# Revit family: Indoor_Pendant Lamp_Santa&Cole_M64
name_source: partatom
category: Luminarias
revit_build: Autodesk Revit 2018 (Build: 20190510_1515(x64)
units: mm (PartAtom-declared; Revit-internal decimal feet)

## family parameters
Anfitrión = Cara
Compartido = No
Corte con vacíos al cargar = No
Cota de conector redondo = Diámetro de uso
Origen de luz = Sí
Punto de cálculo de habitación = No
Tipo de pieza = Normal

## types (5) — shared parameters
Assembly Instructions - CE = https://www.santacole.com
Assembly Instructions - UL = https://www.santacole.com
Cambio de temperatura de color de luz atenuada = <Ninguno>
Carga aparente = 8 W
Code = HEFxx+HEL0x+M640x
Elevación por defecto = 1219 mm
Energy Label = https://www.santacole.com
Fabricante = Santa & Cole
Filtro de color = 16777215
Load = 10 W
Manufacturer website = http://www.santacole.com
Modelo = M64
Technical Information = https://www.santacole.com
URL = https://www.santacole.com
Voltaje (90-305 V) = 220 V
Weight = 1.00 kg
Ángulo de inclinación = -90.00°

## per-type parameters (varying)
| type | Archivo de red fotométrica | Lamp Shade Material | Lámpara |
| M64 - Polished Aluminium | M6403.IES | M64 Lamp Shade : Polished Aluminium |  |
| M64 - Brass | M6403.IES | M64 Lamp Shade : Brass | Head LED |
| M64 - Black Matte Aluminium | M6403.IES | M64 Lamp Shade : Black Matte Aluminium | Head LED |
| M64 - White Matte Aluminium | M6403.IES | M64 Lamp Shade : White Matte Aluminium | Head LED |
| M64 - Brilliant Red Aluminium | M6401_350mA.IES | M64 Lamp Shade : Brilliant Red Aluminium | Head LED |

## geometry (parser evidence)
native form markers: Blend x4, Sweep x7
no freeform markers — native parametric forms only
